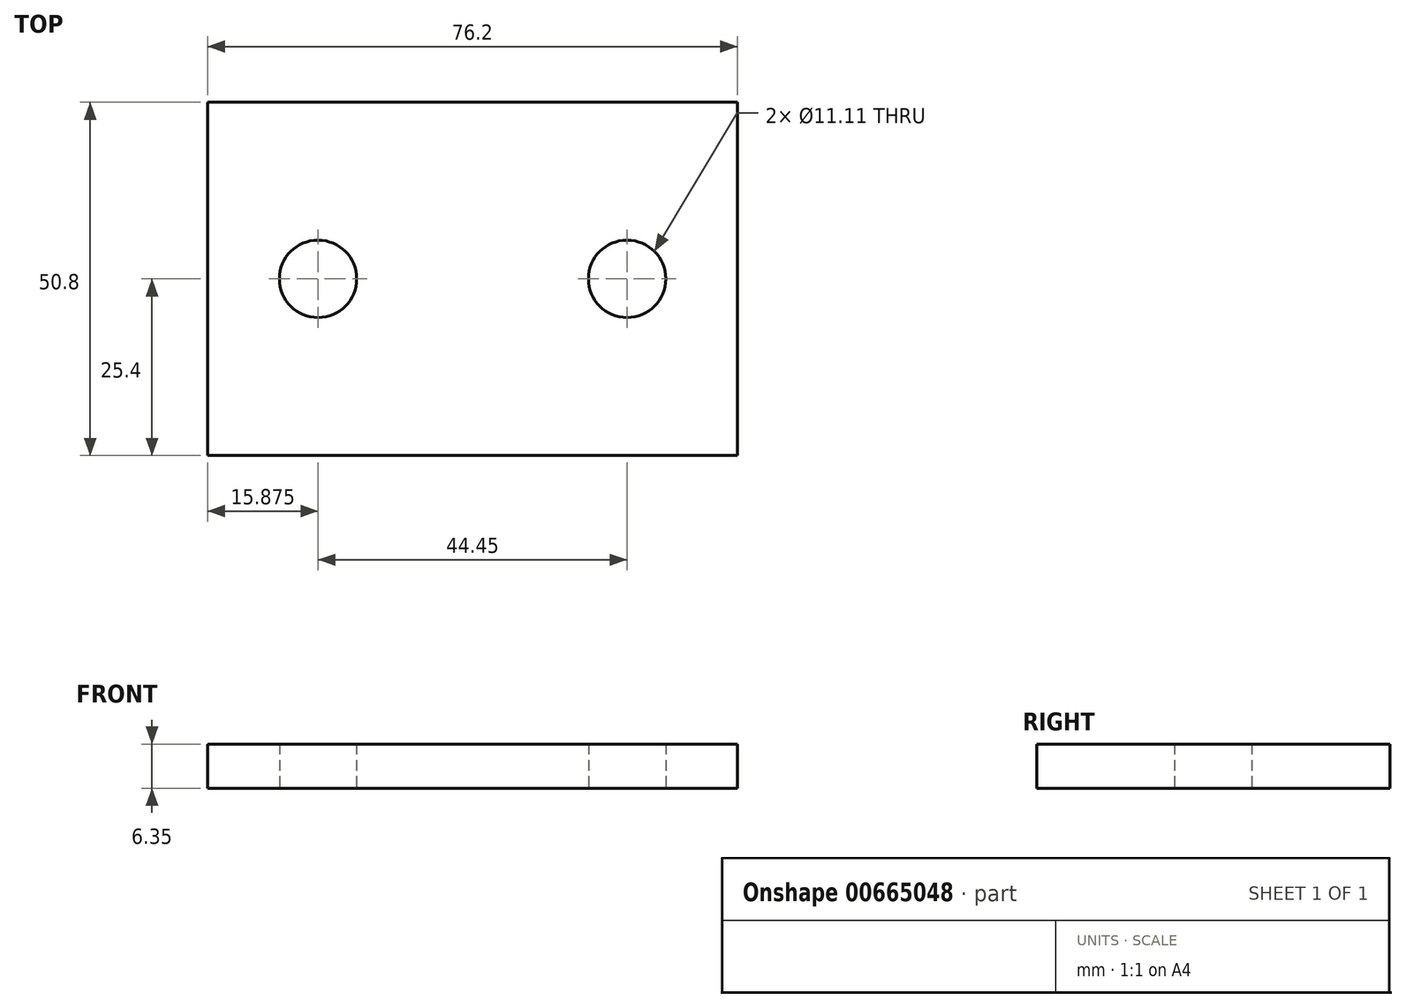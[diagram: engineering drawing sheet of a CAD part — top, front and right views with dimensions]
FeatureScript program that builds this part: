
annotation { "Feature Type Name" : "Feature", "Feature Type Description" : "" }
export const myFeature = defineFeature(function(context is Context, id is Id, definition is map)
    precondition{}
    {
        {
            var Q0;
            Q0=qCreatedBy(makeId("Top.planeOp"),FACE);
            var sketch = newSketch(context, id + "F0", { "sketchPlane" : qUnion([Q0])});
            skLineSegment(sketch, "E0.bottom", {"start": v(38.1, 25.4) * mm, "end": v(-38.1, 25.4) * mm});
            skLineSegment(sketch, "E0.top", {"start": v(38.1, -25.4) * mm, "end": v(-38.1, -25.4) * mm});
            skLineSegment(sketch, "E0.left", {"start": v(38.1, 25.4) * mm, "end": v(38.1, -25.4) * mm});
            skLineSegment(sketch, "E0.right", {"start": v(-38.1, 25.4) * mm, "end": v(-38.1, -25.4) * mm});
            skPoint(sketch, "E0.middle", {"position": v(0, 0) * mm});
            skCircle(sketch, "E1", {"center": v(-22.23, 0) * mm, "radius": 5.56 * mm});
            skCircle(sketch, "E2", {"center": v(22.23, 0) * mm, "radius": 5.56 * mm});
            skSolve(sketch);
        }
        {
            var Q0;
            Q0=makeQuery(id+"F0.imprint","IMPRINT",FACE,{"disambiguationData":[TD([[makeQuery(id+"F0.imprint","IMPRINT",EDGE,{"derivedFrom":sQuery(id+"F0.wireOp",EDGE,"E0.bottom")}),1.0]])]});
            extrude(context, id + "F1", {"entities" : qUnion([Q0]), "depth" : 6.35 * mm, "offsetDistance" : 25.4 * mm});
        }
    });
